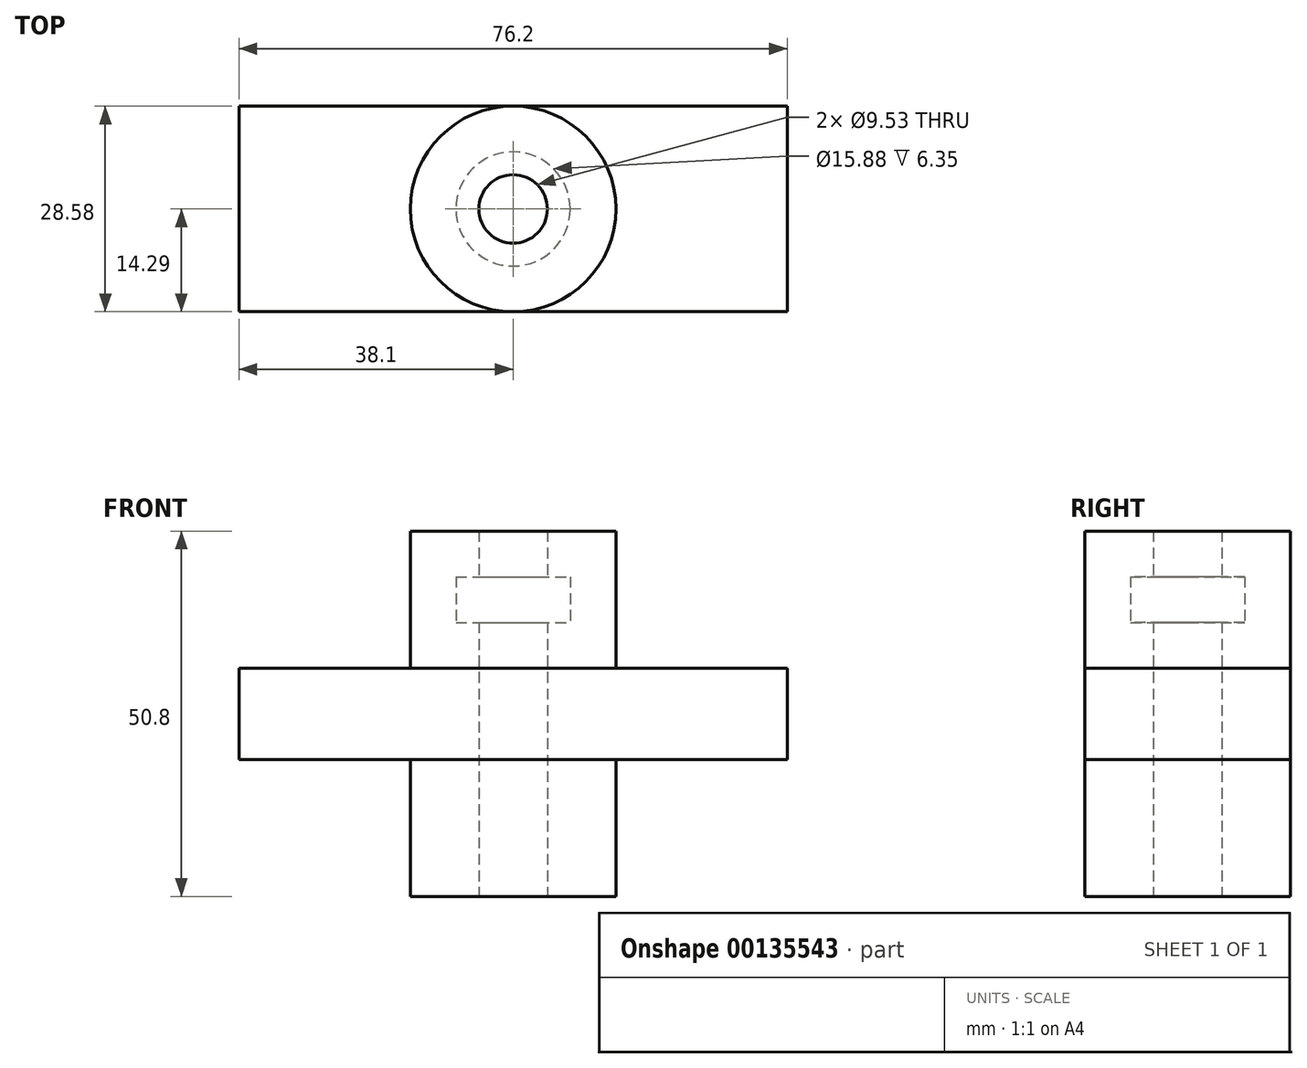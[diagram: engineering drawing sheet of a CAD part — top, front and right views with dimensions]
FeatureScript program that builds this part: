
annotation { "Feature Type Name" : "Feature", "Feature Type Description" : "" }
export const myFeature = defineFeature(function(context is Context, id is Id, definition is map)
    precondition{}
    {
        {
            var Q0;
            Q0=qCreatedBy(makeId("Front.planeOp"),FACE);
            var sketch = newSketch(context, id + "F0", { "sketchPlane" : qUnion([Q0])});
            skLineSegment(sketch, "E0", {"start": v(0, -27.3) * mm, "end": v(0, 38.4) * mm, "construction": true});
            skLineSegment(sketch, "E1", {"start": v(-4.76, 50.8) * mm, "end": v(-14.29, 50.8) * mm});
            skLineSegment(sketch, "E2", {"start": v(-14.29, 50.8) * mm, "end": v(-14.29, 0) * mm});
            skLineSegment(sketch, "E3", {"start": v(-14.29, 0) * mm, "end": v(-4.76, 0) * mm});
            skLineSegment(sketch, "E4", {"start": v(-4.76, 0) * mm, "end": v(-4.76, 38.1) * mm});
            skLineSegment(sketch, "E5", {"start": v(-4.76, 38.1) * mm, "end": v(-7.94, 38.1) * mm});
            skLineSegment(sketch, "E6", {"start": v(-7.94, 38.1) * mm, "end": v(-7.94, 44.45) * mm});
            skLineSegment(sketch, "E7", {"start": v(-7.94, 44.45) * mm, "end": v(-4.76, 44.45) * mm});
            skLineSegment(sketch, "E8", {"start": v(-4.76, 44.45) * mm, "end": v(-4.76, 50.8) * mm});
            skSolve(sketch);
        }
        {
            var Q0;
            Q0 = qSketchRegion(id + "F0", true);
            var Q1;
            Q1=sQuery(id+"F0.wireOp",EDGE,"E0");
            revolve(context, id + "F1", {"entities" : qUnion([Q0]), "axis" : qUnion([Q1]), "revolveType" : RevolveType.FULL});
        }
        {
            var Q0;
            Q0=qCreatedBy(makeId("Top.planeOp"),FACE);
            cPlane(context, id + "F2", {"entities" : qUnion([Q0]), "cplaneType" : CPlaneType.OFFSET, "offset" : 19.05 * mm, "width" : 152.4 * mm, "height" : 152.4 * mm});
        }
        {
            var Q0;
            Q0=qCreatedBy(id+"F2.planeOp",FACE);
            var sketch = newSketch(context, id + "F3", { "sketchPlane" : qUnion([Q0])});
            skLineSegment(sketch, "E9.bottom", {"start": v(-38.1, 14.29) * mm, "end": v(38.1, 14.29) * mm});
            skLineSegment(sketch, "E9.top", {"start": v(-38.1, -14.29) * mm, "end": v(38.1, -14.29) * mm});
            skLineSegment(sketch, "E9.left", {"start": v(-38.1, 14.29) * mm, "end": v(-38.1, -14.29) * mm});
            skLineSegment(sketch, "E9.right", {"start": v(38.1, 14.29) * mm, "end": v(38.1, -14.29) * mm});
            skCircle(sketch, "E10.0", {"center": v(0, 0) * mm, "radius": 14.29 * mm});
            skSolve(sketch);
        }
        {
            var Q0;
            Q0 = qSketchRegion(id + "F3", true);
            extrude(context, id + "F4", {"entities" : qUnion([Q0]), "operationType" : NewBodyOperationType.ADD, "depth" : 12.7 * mm});
        }
        {
            var Q0;
            Q0=makeQuery(id+"F1.opRevolve","SWEPT_FACE",FACE,{"disambiguationData":[OSD([sQuery(id+"F0.wireOp",EDGE,"E1")])]});
            var sketch = newSketch(context, id + "F5", { "sketchPlane" : qUnion([Q0])});
            skCircle(sketch, "E11.0", {"center": v(0, 0) * mm, "radius": 4.76 * mm});
            skSolve(sketch);
        }
        {
            var Q0;
            Q0 = qSketchRegion(id + "F5", true);
            extrude(context, id + "F6", {"entities" : qUnion([Q0]), "operationType" : NewBodyOperationType.REMOVE, "endBound" : BoundingType.THROUGH_ALL, "oppositeDirection" : true, "depth" : 25.4 * mm});
        }
    });
